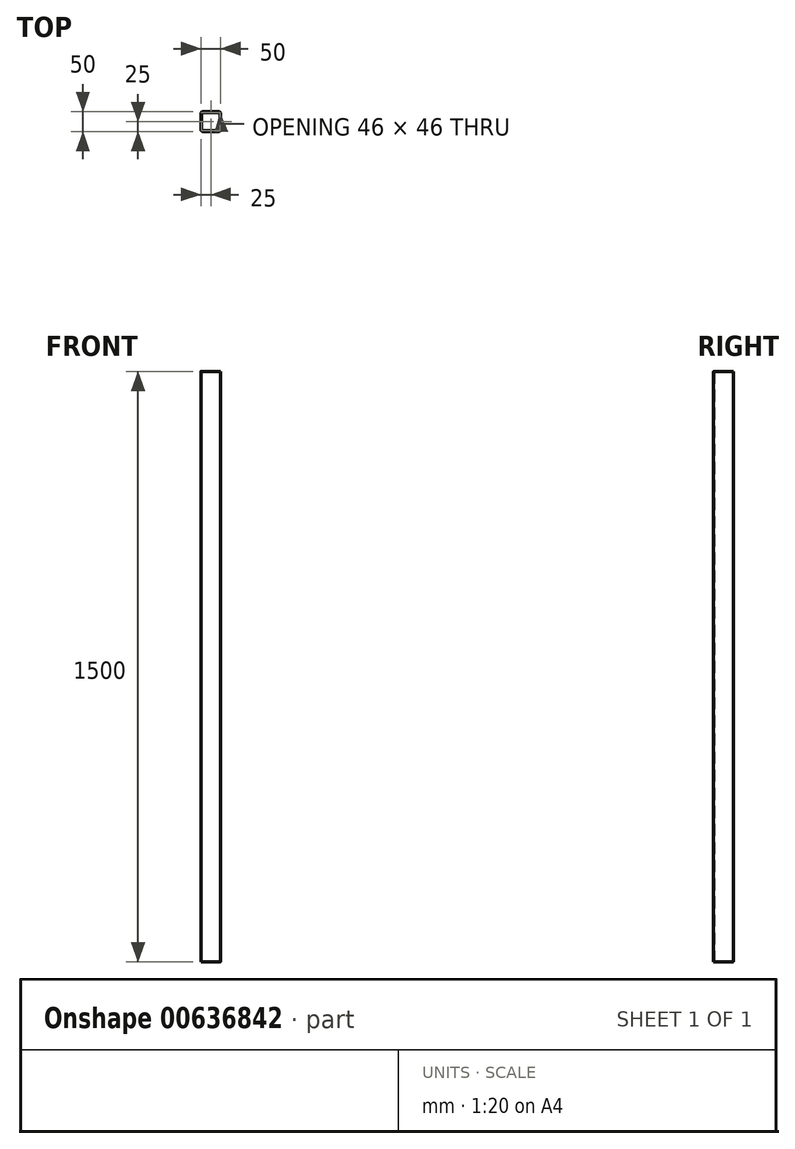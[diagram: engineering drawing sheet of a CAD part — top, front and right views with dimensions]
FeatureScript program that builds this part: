
annotation { "Feature Type Name" : "Feature", "Feature Type Description" : "" }
export const myFeature = defineFeature(function(context is Context, id is Id, definition is map)
    precondition{}
    {
        {
            var Q0;
            Q0=qCreatedBy(makeId("Top.planeOp"),FACE);
            var sketch = newSketch(context, id + "F0", { "sketchPlane" : qUnion([Q0])});
            skLineSegment(sketch, "E0.bottom", {"start": v(21, -25) * mm, "end": v(-21, -25) * mm});
            skLineSegment(sketch, "E0.top", {"start": v(21, 25) * mm, "end": v(-21, 25) * mm});
            skLineSegment(sketch, "E0.left", {"start": v(25, -21) * mm, "end": v(25, 21) * mm});
            skLineSegment(sketch, "E0.right", {"start": v(-25, -21) * mm, "end": v(-25, 21) * mm});
            skPoint(sketch, "E0.middle", {"position": v(0, 0) * mm});
            skLineSegment(sketch, "E1.0", {"start": v(21, 23) * mm, "end": v(-21, 23) * mm});
            skLineSegment(sketch, "E2.0", {"start": v(23, -21) * mm, "end": v(23, 21) * mm});
            skLineSegment(sketch, "E3.0", {"start": v(21, -23) * mm, "end": v(-21, -23) * mm});
            skLineSegment(sketch, "E4.0", {"start": v(-23, -21) * mm, "end": v(-23, 21) * mm});
            skArc(sketch, "E5.filletArc", {"start": v(-21, 23) * mm, "mid": v(-22.41, 22.41) * mm, "end": v(-23, 21) * mm});
            skPoint(sketch, "E6.visualSharp", {"position": v(-25, 25) * mm});
            skArc(sketch, "E6.filletArc", {"start": v(-21, 25) * mm, "mid": v(-23.83, 23.83) * mm, "end": v(-25, 21) * mm});
            skArc(sketch, "E7.filletArc", {"start": v(23, 21) * mm, "mid": v(22.41, 22.41) * mm, "end": v(21, 23) * mm});
            skArc(sketch, "E8.filletArc", {"start": v(21, -23) * mm, "mid": v(22.41, -22.41) * mm, "end": v(23, -21) * mm});
            skArc(sketch, "E9.filletArc", {"start": v(-23, -21) * mm, "mid": v(-22.41, -22.41) * mm, "end": v(-21, -23) * mm});
            skPoint(sketch, "E10.visualSharp", {"position": v(-25, -25) * mm});
            skArc(sketch, "E10.filletArc", {"start": v(-25, -21) * mm, "mid": v(-23.83, -23.83) * mm, "end": v(-21, -25) * mm});
            skPoint(sketch, "E11.visualSharp", {"position": v(25, -25) * mm});
            skArc(sketch, "E11.filletArc", {"start": v(21, -25) * mm, "mid": v(23.83, -23.83) * mm, "end": v(25, -21) * mm});
            skPoint(sketch, "E12.visualSharp", {"position": v(25, 25) * mm});
            skArc(sketch, "E12.filletArc", {"start": v(25, 21) * mm, "mid": v(23.83, 23.83) * mm, "end": v(21, 25) * mm});
            skSolve(sketch);
        }
        {
            var Q0;
            Q0 = qSketchRegion(id + "F0", true);
            extrude(context, id + "F1", {"entities" : qUnion([Q0]), "depth" : 1500 * mm, "offsetDistance" : 25 * mm});
        }
    });
